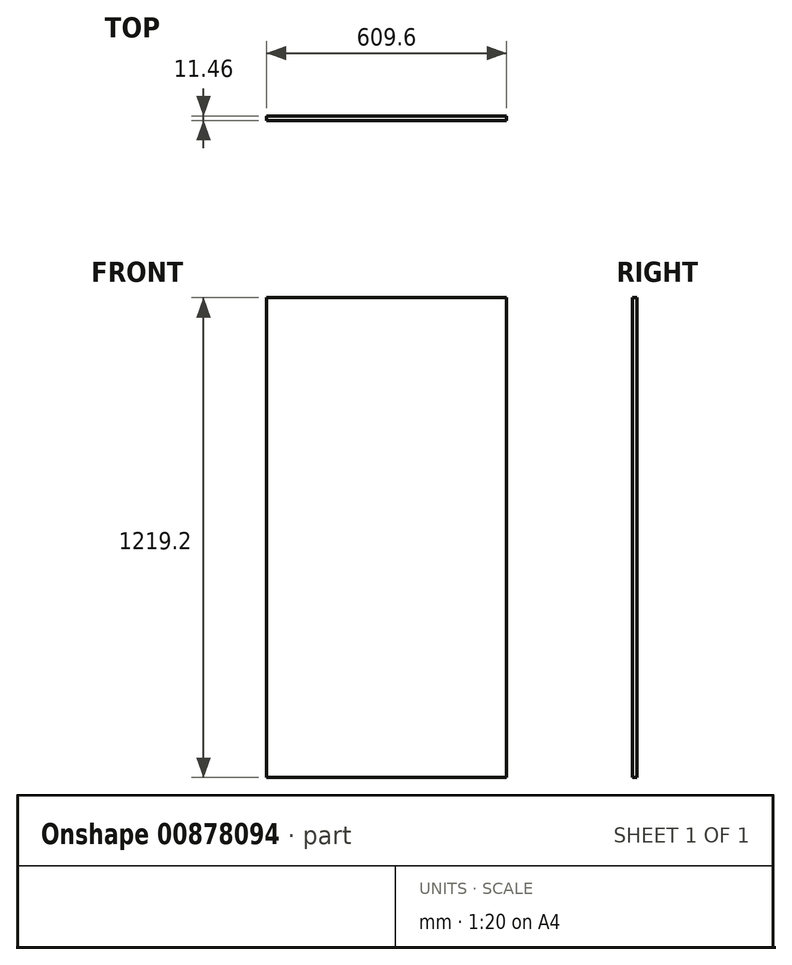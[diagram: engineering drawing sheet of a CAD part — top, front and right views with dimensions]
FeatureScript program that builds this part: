
annotation { "Feature Type Name" : "Feature", "Feature Type Description" : "" }
export const myFeature = defineFeature(function(context is Context, id is Id, definition is map)
    precondition{}
    {
        {
            var Q0;
            Q0=qCreatedBy(makeId("Front.planeOp"),FACE);
            var sketch = newSketch(context, id + "F0", { "sketchPlane" : qUnion([Q0])});
            skLineSegment(sketch, "E0.bottom", {"start": v(-304.8, 609.6) * mm, "end": v(304.8, 609.6) * mm});
            skLineSegment(sketch, "E0.top", {"start": v(-304.8, -609.6) * mm, "end": v(304.8, -609.6) * mm});
            skLineSegment(sketch, "E0.left", {"start": v(-304.8, 609.6) * mm, "end": v(-304.8, -609.6) * mm});
            skLineSegment(sketch, "E0.right", {"start": v(304.8, 609.6) * mm, "end": v(304.8, -609.6) * mm});
            skPoint(sketch, "E0.middle", {"position": v(0, 0) * mm});
            skSolve(sketch);
        }
        {
            var Q0;
            Q0=makeQuery(id+"F0.imprint","IMPRINT",FACE,{"disambiguationData":[TD([[makeQuery(id+"F0.imprint","IMPRINT",EDGE,{"derivedFrom":sQuery(id+"F0.wireOp",EDGE,"E0.bottom")}),-1.0]])]});
            extrude(context, id + "F1", {"entities" : qUnion([Q0]), "endBound" : BoundingType.SYMMETRIC, "depth" : 11.46 * mm, "offsetDistance" : 25.4 * mm});
        }
    });
